# Revit family: T200188
name_source: partatom
category: Furniture
revit_build: Autodesk Revit Architecture 2015 (Build: 20140322_1515(x64)
units: mm (PartAtom-declared; Revit-internal decimal feet)

## types (1)
- T200188
    Assembly Code = E2020400
    Catalog = https://ofs.com
    Description = OFS TYPICAL T200188
    Manufacturer = OFS
    Model = T200188
    Staks Benching Toolrail = STACKS TOOLRAIL PAINT
    Staks Frosted Acrylic Shelf = OFS STAKS Frosted Glass
    Staks Mobile Pedestal Chasis = OFS STAKS Chasis Wood Grain Laminate
    Staks Mobile Pedestal Drawer = OFS STAKS Drawer Front Material
    Staks Mobile Pedestal Drawer handle = OFS STAKS Handle Material
    Staks Mobile Pedestal Top Surface = OFS STAKS Chasis Wood Grain Laminate
    Staks Mobile Pedestal Wheel = OFS STAKS Plastic
    Staks Seat Cushion = OFS STAKS Cushion Material
    Staks Support Center H = STACKS PAINT
    URL = https://ofs.com

## geometry (parser evidence)
native form markers: Blend x88, Sweep x22
no freeform markers — native parametric forms only
